# Revit family: Wood_Frame_CB-540_BIM
name_source: partatom
category: Arredi
units: mm (PartAtom-declared; Revit-internal decimal feet)

## family parameters
Attiva taglio nelle viste = No
Basato su piano di lavoro = No
Condiviso = No
Numero OmniClass = 23.40.20.00
Origine composizione di rendering = Geometria famiglia
Punto di calcolo locali = No
Sempre verticale = Sì
Taglio con vuoti quando caricato = No
Titolo OmniClass = General Furniture and Specialties

## types (1)
- CB-540
    AVAILABLE FINISHES = Ebonized black lacquer on Ash (EB) or bleached, white pigment, matte acrylic on Ash (BL). Raw effect lacquer on Oak (RE). Hand rubbed natural oil on Oak or Walnut (NA), or hand rubbed black oil on Walnut (BO).
    BASE MATERIAL = BASSAM_FELLOWS_COMFORT_LEATHER_43632_CAMEL
    BIM BADGE = https://bim.archiproducts.com
    COLLECTION = Wood Frame
    DEPTH = 622 mm
    Descrizione = Wood and upholstered chair with armrests
    HEIGHT = 787 mm
    MATERIAL DESCRIPTION = Solid wood frame. Upholstery: dual density foam with inverted seams, tufted and welted.
    Modello = Wood Frame Armchair
    PRODUCT CODE = CB-540
    PRODUCT SHEET = https://www.archiproducts.com
    Produttore = BassamFellows
    Prospetto di default = 0 mm  [stored 0 ft]
    STRUCTURE MATERIAL = BASSAM_FELLOWS_WALNUT_BLACK_OIL_W-BO
    TECHNICAL SHEET = https://bassamfellows.com
    UPHOLSTERY MATERIAL = BASSAM_FELLOWS_COMFORT_LEATHER_43632_CAMEL
    URL = https://bassamfellows.com
    WIDTH = 610 mm

note: [stored X ft] marks values corroborated as IEEE doubles in the binary element streams (Revit-internal decimal feet)

## geometry (parser evidence)
native form markers: Sweep x1
no freeform markers — native parametric forms only
